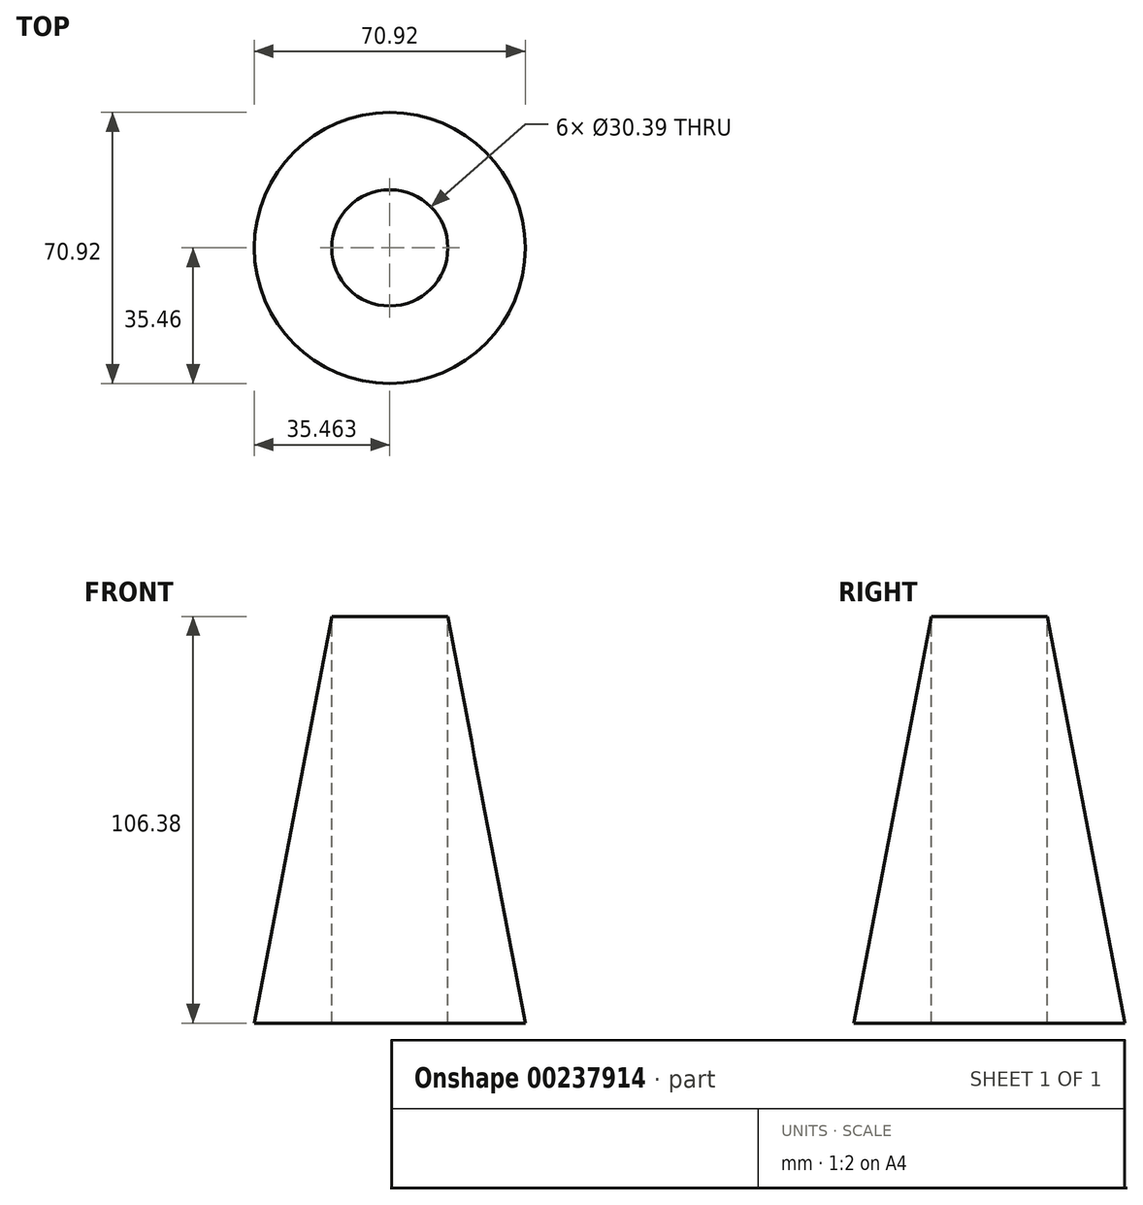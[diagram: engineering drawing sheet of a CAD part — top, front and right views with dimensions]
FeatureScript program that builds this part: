
annotation { "Feature Type Name" : "Feature", "Feature Type Description" : "" }
export const myFeature = defineFeature(function(context is Context, id is Id, definition is map)
    precondition{}
    {
        {
            var Q0;
            Q0=qCreatedBy(makeId("Front.planeOp"),FACE);
            var sketch = newSketch(context, id + "F0", { "sketchPlane" : qUnion([Q0])});
            skLineSegment(sketch, "E0", {"start": v(-34.12, 57.96) * mm, "end": v(-34.12, -48.42) * mm});
            skLineSegment(sketch, "E1", {"start": v(-34.12, -48.42) * mm, "end": v(-13.86, -48.42) * mm});
            skLineSegment(sketch, "E2", {"start": v(-34.12, 57.96) * mm, "end": v(-13.86, -48.42) * mm});
            skSolve(sketch);
        }
        {
            var Q0;
            Q0=qCreatedBy(makeId("Front.planeOp"),FACE);
            var sketch = newSketch(context, id + "F1", { "sketchPlane" : qUnion([Q0])});
            skLineSegment(sketch, "E3", {"start": v(-49.32, 57.06) * mm, "end": v(-49.32, -48.42) * mm});
            skSolve(sketch);
        }
        {
            var Q0;
            Q0=makeQuery(id+"F0.imprint","IMPRINT",FACE,{"disambiguationData":[TD([[makeQuery(id+"F0.imprint","IMPRINT",EDGE,{"derivedFrom":sQuery(id+"F0.wireOp",EDGE,"E0")}),1.0]])]});
            var Q1;
            Q1=sQuery(id+"F1.wireOp",EDGE,"E3");
            revolve(context, id + "F2", {"entities" : qUnion([Q0]), "axis" : qUnion([Q1]), "revolveType" : RevolveType.FULL});
        }
    });
